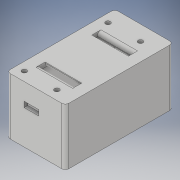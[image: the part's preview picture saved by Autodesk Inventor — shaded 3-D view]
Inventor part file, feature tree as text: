
AUTODESK INVENTOR PART (.ipt)
format: ipt  version: 2017.3 (Build 213257000, 257)  size: 175,616 bytes
history: native  units: mm
features: sketch x5, extrude x4, fillet x3, hole x1
ambient origin geometry x8: Origin, YZ Plane, XZ Plane, XY Plane, X Axis, Y Axis, Z Axis, Center Point
bodies: Volumenkörper1 (feature_tree)
feature tree (13):
  extrude  "Extrusion1"  Depth=59.0mm
  extrude  "Extrusion2"  Depth=2.0mm
  extrude  "Extrusion5"  Depth=2.0mm
  extrude  "Extrusion6"  Depth=28.5mm TaperAngle=0.0deg
  fillet  "Rundung1"  Radius=3.0mm
  fillet  "Rundung2"  Radius=20.0mm
  fillet  "Rundung3"  Radius=3.0mm
  hole  "Bohrung4"  [1 undecoded]
  sketch  "Skizze1"  dims[d0=32.0mm d1=59.0mm]
  sketch  "Skizze2"  dims[d2=31.0mm d3=0.0mm d4=2.0mm]
  sketch  "Skizze8"  dims[d5=2.0mm d6=2.0mm]
  sketch  "Skizze9"  dims[d7=2.0mm d8=28.5mm d9=0.0mm d43=3.0mm d44=20.0mm d46=3.0mm]
  sketch  "Skizze11"  dims[d47=20.0mm d49=3.5mm d50=0.0mm d54=8.0mm d55=3.0mm d57=3.5mm d58=0.0mm d67=2.0mm d68=2.0mm d69=2.0mm d70=6.8mm d71=10.0mm d72=13.5mm d74=2.6mm d75=6.0mm d76=4.0mm d77=2.0mm d78=90.0deg d79=8.0mm d80=20.594885mm d81=7.5mm d82=4.61mm d83=5.0mm d84=45.72mm d85=17.78mm]
note: 1 required parameter value undecoded (feature->parameter linkage not recoverable at this tier; creation-order binding heuristic only, values carry confidence <= 0.55)
